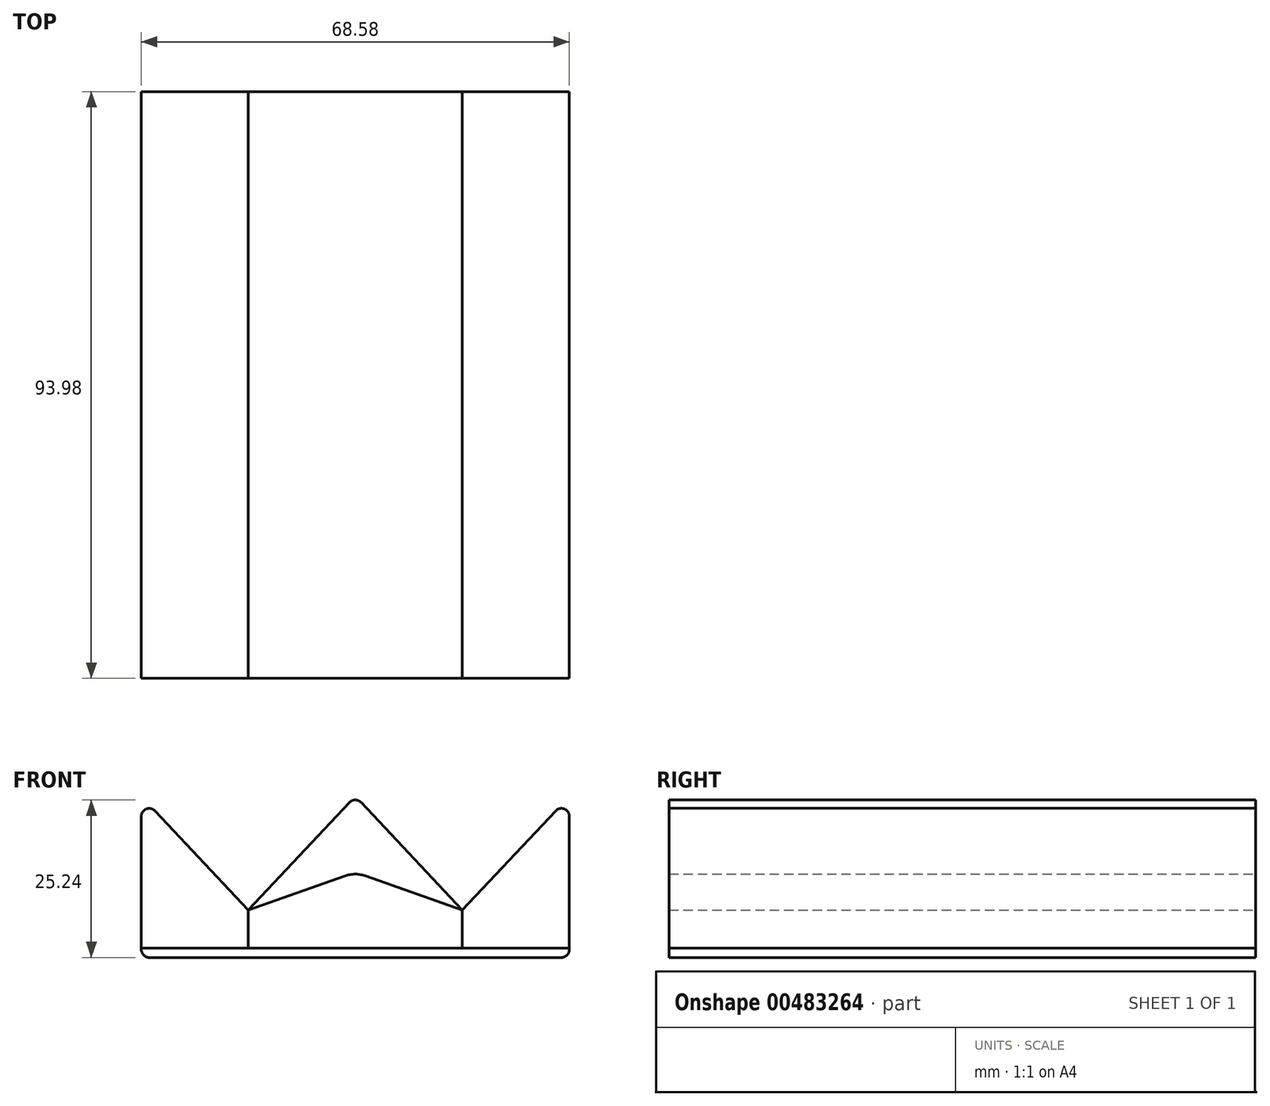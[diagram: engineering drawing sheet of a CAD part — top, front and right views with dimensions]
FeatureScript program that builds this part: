
annotation { "Feature Type Name" : "Feature", "Feature Type Description" : "" }
export const myFeature = defineFeature(function(context is Context, id is Id, definition is map)
    precondition{}
    {
        {
            var Q0;
            Q0=qCreatedBy(makeId("Front.planeOp"),FACE);
            var sketch = newSketch(context, id + "F0", { "sketchPlane" : qUnion([Q0])});
            skLineSegment(sketch, "E0.bottom", {"start": v(-34.3, 12.16) * mm, "end": v(34.3, 12.16) * mm});
            skLineSegment(sketch, "E0.top", {"start": v(-34.3, -12.16) * mm, "end": v(34.3, -12.16) * mm});
            skLineSegment(sketch, "E0.left", {"start": v(-34.3, 12.16) * mm, "end": v(-34.3, -12.16) * mm});
            skLineSegment(sketch, "E0.right", {"start": v(34.3, 12.16) * mm, "end": v(34.3, -12.16) * mm});
            skPoint(sketch, "E0.middle", {"position": v(0, 0) * mm});
            skLineSegment(sketch, "E1", {"start": v(34.3, -12.16) * mm, "end": v(0, 0) * mm});
            skLineSegment(sketch, "E2", {"start": v(-34.3, -12.16) * mm, "end": v(0, 0) * mm});
            skLineSegment(sketch, "E3", {"start": v(-17.15, -6.08) * mm, "end": v(-34.3, 12.16) * mm});
            skLineSegment(sketch, "E4", {"start": v(0, 12.16) * mm, "end": v(-17.14, -6.08) * mm});
            skLineSegment(sketch, "E5", {"start": v(0, 12.16) * mm, "end": v(17.14, -6.08) * mm});
            skLineSegment(sketch, "E6", {"start": v(17.15, -6.08) * mm, "end": v(34.3, 12.16) * mm});
            skLineSegment(sketch, "E7", {"start": v(-17.15, -6.08) * mm, "end": v(-17.15, -12.16) * mm});
            skLineSegment(sketch, "E8", {"start": v(17.15, -6.08) * mm, "end": v(17.15, -12.16) * mm});
            skLineSegment(sketch, "E9", {"start": v(-34.3, -12.16) * mm, "end": v(-34.3, -13.66) * mm});
            skLineSegment(sketch, "E10", {"start": v(-34.3, -13.66) * mm, "end": v(34.3, -13.66) * mm});
            skLineSegment(sketch, "E11", {"start": v(34.3, -13.66) * mm, "end": v(34.3, -12.16) * mm});
            skSolve(sketch);
        }
        {
            var Q0;
            {var subQ0=sQuery(id+"F0.wireOp",EDGE,"E0.left");Q0=makeQuery(id+"F0.imprint","IMPRINT",FACE,{"disambiguationData":[TD([[makeQuery(id+"F0.imprint","IMPRINT",EDGE,{"derivedFrom":subQ0}),1.0]])]});}
            var Q1;
            {var subQ3=sQuery(id+"F0.wireOp",EDGE,"E7");Q1=makeQuery(id+"F0.imprint","IMPRINT",FACE,{"disambiguationData":[TD([[makeQuery(id+"F0.imprint","IMPRINT",EDGE,{"derivedFrom":subQ3}),-1.0]])]});}
            var Q2;
            {var subQ3=sQuery(id+"F0.wireOp",EDGE,"E8");Q2=makeQuery(id+"F0.imprint","IMPRINT",FACE,{"disambiguationData":[TD([[makeQuery(id+"F0.imprint","IMPRINT",EDGE,{"derivedFrom":subQ3}),1.0]])]});}
            var Q3;
            {var subQ0=sQuery(id+"F0.wireOp",EDGE,"E0.right");Q3=makeQuery(id+"F0.imprint","IMPRINT",FACE,{"disambiguationData":[TD([[makeQuery(id+"F0.imprint","IMPRINT",EDGE,{"derivedFrom":subQ0}),-1.0]])]});}
            var Q4;
            {var subQ4=sQuery(id+"F0.wireOp",EDGE,"E4");Q4=makeQuery(id+"F0.imprint","IMPRINT",FACE,{"disambiguationData":[TD([[makeQuery(id+"F0.imprint","IMPRINT",EDGE,{"derivedFrom":subQ4}),1.0]])]});}
            extrude(context, id + "F1", {"entities" : qUnion([Q0, Q1, Q2, Q3, Q4]), "depth" : 93.98 * mm});
        }
        {
            var Q0;
            Q0=sQuery(id+"F0.wireOp",EDGE,"E0.top");
            extrude(context, id + "F2", {"bodyType" : ToolBodyType.SURFACE, "surfaceEntities" : qUnion([Q0]), "depth" : 93.98 * mm});
        }
        {
            var Q0;
            {var subQ4=sQuery(id+"F0.wireOp",EDGE,"E9");Q0=makeQuery(id+"F0.imprint","IMPRINT",FACE,{"disambiguationData":[TD([[makeQuery(id+"F0.imprint","IMPRINT",EDGE,{"derivedFrom":subQ4}),1.0]])]});}
            extrude(context, id + "F3", {"entities" : qUnion([Q0]), "depth" : 93.98 * mm});
        }
        {
            var Q0;
            Q0=makeQuery(id+"F1.opExtrude","SWEPT_EDGE",EDGE,{"disambiguationData":[OSD([sQuery(id+"F0.wireOp",EDGE,"E1"),sQuery(id+"F0.wireOp",EDGE,"E2")])]});
            fillet(context, id + "F4", {"entities" : qUnion([Q0]), "radius" : 5.08 * mm, "tangentPropagation" : true, "allowEdgeOverflow" : false});
        }
        {
            var Q0;
            Q0=makeQuery(id+"F1.opExtrude","SWEPT_EDGE",EDGE,{"disambiguationData":[OSD([sQuery(id+"F0.wireOp",EDGE,"E0.bottom"),sQuery(id+"F0.wireOp",EDGE,"E0.left"),sQuery(id+"F0.wireOp",EDGE,"E3")])]});
            fillet(context, id + "F5", {"entities" : qUnion([Q0]), "radius" : 1.27 * mm, "tangentPropagation" : true, "allowEdgeOverflow" : false});
        }
        {
            var Q0;
            Q0=makeQuery(id+"F1.opExtrude","SWEPT_EDGE",EDGE,{"disambiguationData":[OSD([sQuery(id+"F0.wireOp",EDGE,"E0.bottom"),sQuery(id+"F0.wireOp",EDGE,"E0.right"),sQuery(id+"F0.wireOp",EDGE,"E6")])]});
            var Q1;
            Q1=makeQuery(id+"F1.opExtrude","SWEPT_EDGE",EDGE,{"disambiguationData":[OSD([sQuery(id+"F0.wireOp",EDGE,"E0.bottom"),sQuery(id+"F0.wireOp",EDGE,"E4"),sQuery(id+"F0.wireOp",EDGE,"E5")])]});
            var Q2;
            Q2=makeQuery(id+"F3.opExtrude","SWEPT_EDGE",EDGE,{"disambiguationData":[OSD([sQuery(id+"F0.wireOp",EDGE,"E9"),sQuery(id+"F0.wireOp",EDGE,"E10")])]});
            var Q3;
            Q3=makeQuery(id+"F3.opExtrude","SWEPT_EDGE",EDGE,{"disambiguationData":[OSD([sQuery(id+"F0.wireOp",EDGE,"E10"),sQuery(id+"F0.wireOp",EDGE,"E11")])]});
            fillet(context, id + "F6", {"entities" : qUnion([Q0, Q1, Q2, Q3]), "radius" : 1.27 * mm, "tangentPropagation" : true, "allowEdgeOverflow" : false});
        }
    });
